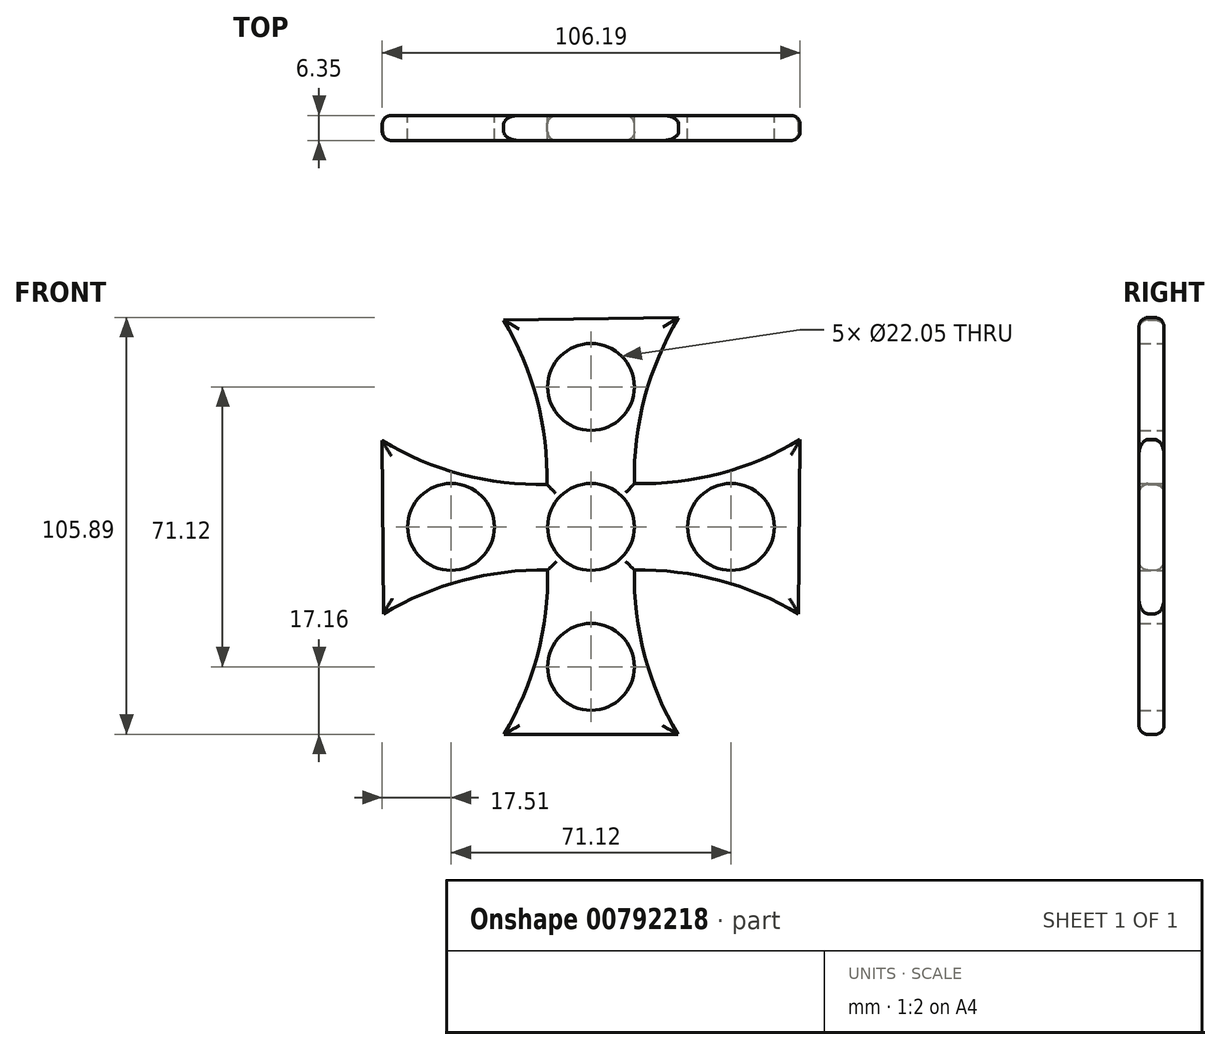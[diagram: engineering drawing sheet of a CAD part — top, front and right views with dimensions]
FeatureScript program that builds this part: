
annotation { "Feature Type Name" : "Feature", "Feature Type Description" : "" }
export const myFeature = defineFeature(function(context is Context, id is Id, definition is map)
    precondition{}
    {
        {
            var Q0;
            Q0=qCreatedBy(makeId("Front.planeOp"),FACE);
            var sketch = newSketch(context, id + "F0", { "sketchPlane" : qUnion([Q0])});
            skArc(sketch, "E0", {"start": v(11.01, -10.99) * mm, "mid": v(13.6, -32.63) * mm, "end": v(22.03, -52.72) * mm});
            skArc(sketch, "E1", {"start": v(-22.1, -52.7) * mm, "mid": v(-13.64, -32.62) * mm, "end": v(-11.04, -10.99) * mm});
            skArc(sketch, "E2", {"start": v(-53.07, 21.89) * mm, "mid": v(-32.9, 13.36) * mm, "end": v(-11.18, 10.75) * mm});
            skArc(sketch, "E3", {"start": v(-11.04, -10.99) * mm, "mid": v(-32.68, -13.6) * mm, "end": v(-52.76, -22.07) * mm});
            skArc(sketch, "E4", {"start": v(52.7, -22.09) * mm, "mid": v(32.64, -13.6) * mm, "end": v(11.01, -10.99) * mm});
            skArc(sketch, "E5", {"start": v(11.01, 10.98) * mm, "mid": v(32.86, 13.59) * mm, "end": v(53.12, 22.16) * mm});
            skArc(sketch, "E6", {"start": v(22.25, 53.17) * mm, "mid": v(13.63, 32.87) * mm, "end": v(11.01, 10.98) * mm});
            skArc(sketch, "E7", {"start": v(-11.18, 10.75) * mm, "mid": v(-13.77, 32.42) * mm, "end": v(-22.23, 52.54) * mm});
            skLineSegment(sketch, "E8", {"start": v(-53.07, 21.89) * mm, "end": v(-52.76, -22.07) * mm});
            skLineSegment(sketch, "E9", {"start": v(53.12, 22.16) * mm, "end": v(52.7, -22.09) * mm});
            skLineSegment(sketch, "E10", {"start": v(22.25, 53.17) * mm, "end": v(-22.23, 52.54) * mm});
            skLineSegment(sketch, "E11", {"start": v(-22.1, -52.7) * mm, "end": v(22.03, -52.72) * mm});
            skCircle(sketch, "E12", {"center": v(0, 0) * mm, "radius": 11.02 * mm});
            skSolve(sketch);
        }
        {
            var Q0;
            Q0 = qSketchRegion(id + "F0", true);
            extrude(context, id + "F1", {"entities" : qUnion([Q0]), "depth" : 6.35 * mm, "offsetDistance" : 25.4 * mm});
        }
        {
            var Q0;
            Q0=qCreatedBy(makeId("Front.planeOp"),FACE);
            var sketch = newSketch(context, id + "F2", { "sketchPlane" : qUnion([Q0])});
            skCircle(sketch, "E13", {"center": v(0, 35.56) * mm, "radius": 11.02 * mm});
            skCircle(sketch, "E14", {"center": v(35.56, 0) * mm, "radius": 11.02 * mm});
            skCircle(sketch, "E15", {"center": v(0, -35.56) * mm, "radius": 11.02 * mm});
            skCircle(sketch, "E16", {"center": v(-35.56, 0) * mm, "radius": 11.02 * mm});
            skSolve(sketch);
        }
        {
            var Q0;
            Q0=makeQuery(id+"F1.opExtrude","CAP_EDGE",EDGE,{"disambiguationData":[OSD([sQuery(id+"F0.wireOp",EDGE,"E10")])],"isStart":false});
            var Q1;
            Q1=makeQuery(id+"F1.opExtrude","CAP_EDGE",EDGE,{"disambiguationData":[OSD([sQuery(id+"F0.wireOp",EDGE,"E6")])],"isStart":false});
            var Q2;
            Q2=makeQuery(id+"F1.opExtrude","CAP_EDGE",EDGE,{"disambiguationData":[OSD([sQuery(id+"F0.wireOp",EDGE,"E7")])],"isStart":false});
            var Q3;
            Q3=makeQuery(id+"F1.opExtrude","CAP_EDGE",EDGE,{"disambiguationData":[OSD([sQuery(id+"F0.wireOp",EDGE,"E2")])],"isStart":false});
            var Q4;
            Q4=makeQuery(id+"F1.opExtrude","CAP_EDGE",EDGE,{"disambiguationData":[OSD([sQuery(id+"F0.wireOp",EDGE,"E5")])],"isStart":false});
            var Q5;
            Q5=makeQuery(id+"F1.opExtrude","CAP_EDGE",EDGE,{"disambiguationData":[OSD([sQuery(id+"F0.wireOp",EDGE,"E9")])],"isStart":false});
            var Q6;
            Q6=makeQuery(id+"F1.opExtrude","CAP_EDGE",EDGE,{"disambiguationData":[OSD([sQuery(id+"F0.wireOp",EDGE,"E4")])],"isStart":false});
            var Q7;
            Q7=makeQuery(id+"F1.opExtrude","CAP_EDGE",EDGE,{"disambiguationData":[OSD([sQuery(id+"F0.wireOp",EDGE,"E0")])],"isStart":false});
            var Q8;
            Q8=makeQuery(id+"F1.opExtrude","CAP_EDGE",EDGE,{"disambiguationData":[OSD([sQuery(id+"F0.wireOp",EDGE,"E11")])],"isStart":false});
            var Q9;
            Q9=makeQuery(id+"F1.opExtrude","CAP_EDGE",EDGE,{"disambiguationData":[OSD([sQuery(id+"F0.wireOp",EDGE,"E1")])],"isStart":false});
            var Q10;
            Q10=makeQuery(id+"F1.opExtrude","CAP_EDGE",EDGE,{"disambiguationData":[OSD([sQuery(id+"F0.wireOp",EDGE,"E3")])],"isStart":false});
            var Q11;
            Q11=makeQuery(id+"F1.opExtrude","CAP_EDGE",EDGE,{"disambiguationData":[OSD([sQuery(id+"F0.wireOp",EDGE,"E8")])],"isStart":false});
            var Q12;
            Q12=makeQuery(id+"F1.opExtrude","CAP_EDGE",EDGE,{"disambiguationData":[OSD([sQuery(id+"F0.wireOp",EDGE,"E10")])],"isStart":true});
            var Q13;
            Q13=makeQuery(id+"F1.opExtrude","CAP_EDGE",EDGE,{"disambiguationData":[OSD([sQuery(id+"F0.wireOp",EDGE,"E7")])],"isStart":true});
            var Q14;
            Q14=makeQuery(id+"F1.opExtrude","CAP_EDGE",EDGE,{"disambiguationData":[OSD([sQuery(id+"F0.wireOp",EDGE,"E2")])],"isStart":true});
            var Q15;
            Q15=makeQuery(id+"F1.opExtrude","CAP_EDGE",EDGE,{"disambiguationData":[OSD([sQuery(id+"F0.wireOp",EDGE,"E8")])],"isStart":true});
            var Q16;
            Q16=makeQuery(id+"F1.opExtrude","CAP_EDGE",EDGE,{"disambiguationData":[OSD([sQuery(id+"F0.wireOp",EDGE,"E3")])],"isStart":true});
            var Q17;
            Q17=makeQuery(id+"F1.opExtrude","CAP_EDGE",EDGE,{"disambiguationData":[OSD([sQuery(id+"F0.wireOp",EDGE,"E1")])],"isStart":true});
            var Q18;
            Q18=makeQuery(id+"F1.opExtrude","CAP_EDGE",EDGE,{"disambiguationData":[OSD([sQuery(id+"F0.wireOp",EDGE,"E0")])],"isStart":true});
            var Q19;
            Q19=makeQuery(id+"F1.opExtrude","CAP_EDGE",EDGE,{"disambiguationData":[OSD([sQuery(id+"F0.wireOp",EDGE,"E11")])],"isStart":true});
            var Q20;
            Q20=makeQuery(id+"F1.opExtrude","CAP_EDGE",EDGE,{"disambiguationData":[OSD([sQuery(id+"F0.wireOp",EDGE,"E4")])],"isStart":true});
            var Q21;
            Q21=makeQuery(id+"F1.opExtrude","CAP_EDGE",EDGE,{"disambiguationData":[OSD([sQuery(id+"F0.wireOp",EDGE,"E5")])],"isStart":true});
            var Q22;
            Q22=makeQuery(id+"F1.opExtrude","CAP_EDGE",EDGE,{"disambiguationData":[OSD([sQuery(id+"F0.wireOp",EDGE,"E9")])],"isStart":true});
            var Q23;
            Q23=makeQuery(id+"F1.opExtrude","CAP_EDGE",EDGE,{"disambiguationData":[OSD([sQuery(id+"F0.wireOp",EDGE,"E6")])],"isStart":true});
            fillet(context, id + "F3", {"entities" : qUnion([Q0, Q1, Q2, Q3, Q4, Q5, Q6, Q7, Q8, Q9, Q10, Q11, Q12, Q13, Q14, Q15, Q16, Q17, Q18, Q19, Q20, Q21, Q22, Q23]), "radius" : 2.3 * mm, "tangentPropagation" : true, "allowEdgeOverflow" : false});
        }
        {
            var Q0;
            Q0=makeQuery(id+"F2.imprint","IMPRINT",FACE,{"disambiguationData":[TD([[makeQuery(id+"F2.imprint","IMPRINT",EDGE,{"derivedFrom":sQuery(id+"F2.wireOp",EDGE,"E14")}),1.0]])]});
            var Q1;
            Q1=makeQuery(id+"F2.imprint","IMPRINT",FACE,{"disambiguationData":[TD([[makeQuery(id+"F2.imprint","IMPRINT",EDGE,{"derivedFrom":sQuery(id+"F2.wireOp",EDGE,"E13")}),1.0]])]});
            var Q2;
            Q2=makeQuery(id+"F2.imprint","IMPRINT",FACE,{"disambiguationData":[TD([[makeQuery(id+"F2.imprint","IMPRINT",EDGE,{"derivedFrom":sQuery(id+"F2.wireOp",EDGE,"E16")}),1.0]])]});
            var Q3;
            Q3=makeQuery(id+"F2.imprint","IMPRINT",FACE,{"disambiguationData":[TD([[makeQuery(id+"F2.imprint","IMPRINT",EDGE,{"derivedFrom":sQuery(id+"F2.wireOp",EDGE,"E15")}),1.0]])]});
            extrude(context, id + "F4", {"entities" : qUnion([Q0, Q1, Q2, Q3]), "operationType" : NewBodyOperationType.REMOVE, "endBound" : BoundingType.THROUGH_ALL, "depth" : 25.4 * mm, "offsetDistance" : 25.4 * mm});
        }
    });
